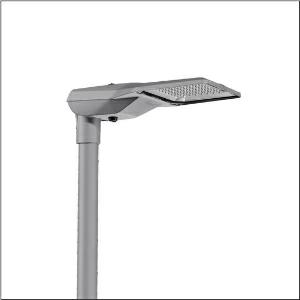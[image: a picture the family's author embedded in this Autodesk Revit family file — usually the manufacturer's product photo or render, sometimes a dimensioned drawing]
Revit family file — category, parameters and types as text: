
# Revit family: streetlight_sl_21_iq_midi___st1_0a_5xe3d61y08mb_8671
name_source: partatom
category: Lighting Fixtures
units: mm (PartAtom-declared; Revit-internal decimal feet)

## family parameters
Cut with Voids When Loaded = No
Host = Face
Light Source = No
Part Type = Normal
Room Calculation Point = No
Round Connector Dimension = Use Diameter
Shared = No

## types (1)
- --- (1 x LED, 15910 lm, 129.3 W, 2700K)
    Apparent Load = 129 VA
    CIE Flux Codes = 37 72 97 100 100
    Color Rendering = 70
    Color Temperature = 2700K
    Default Elevation = 1800 mm
    Description = Streetlight SL 21 iQ midi, mast luminaire, primary light control with lens, of PMMA, primary optical cover: cover, of toughened safety glass, transparent, light distribution: ST1.0a, light emission: direct distribution, primary light characteristic: asymmetric, installation type: post-top, side-entry, LED, High Power LED, rated luminous flux: 15.910lm, luminous efficacy: 123lm/W, light colour: 727, colour temperature: 2700K, control gear: iQ-Street Remote, D4i with power reduction, control: pre-setting: logarithmic dimming characteristic, Street-Remote, Auto-Match, Temp-Guard, Lumen-Switch, Night-Set, Smart-Wire, Light-Fading, Desk-Remote (wireless, voltage-free reading and setting of iQ features in the workshop via application-optimized NFC function/RFID function), optimised constant luminous flux control (CLO 2.0), mains connection: 230..240V, AC, 50/60Hz, start of lifetime: 129W, end of service life: 142W, reduction: 56W, luminaire housing, of diecast aluminium, powder-coated, SITECO metallic grey (DB 702S), corrosivity category C5 high according to DIN EN ISO 12944, please order mast flange separately, inclination adjustable: 0°, 5°, 10°, 15°, sealing non-destructively replaceable, multi-level sealing system, length: 644mm, width: 335mm, height: 110mm, mast flange for spigot size: 42mm (side-entry): 5XC10008XM4, 60/48mm (side-entry/post-top): 5XC10108XM2, 76/60mm (side-entry/post-top): 5XC10108XM1, mounting height: 4..8m, Smart Interface below and above, protection rating (complete): IP66, insulation class (complete): insulation class II (safety insulation), certification: CE, ENEC, ENEC+, VDE, impact resistance: IK10, permissible operating ambient temperature for outdoor applications: -40..+50°C, standard-compliant lighting for roads and squares, packaging unit: 1 piece

Light Distribution: ST1.0a
    Height = 111 mm
    Lamp = 1 x LED
    Lamp Light Flux = 15910 lm
    Lamp Power = 129.3 W
    Lamp count = 1
    Length = 644 mm
    Luminous efficacy = 123 lm/W
    Manufacturer = Siteco
    ModVariant = No
    Model = 5XE3D61Y08MB
    Mounting Place = Pole
    Mounting Type = Pole top
    Number of Poles = 1
    OnlyDefault = Yes
    Power Factor = 1
    Product Name = Streetlight SL 21 iQ midi | ST1.0a
    Product group = mast luminaire | pylon top
    ProductGroupID = 6100
    Protection Class = Protection class II
    Protection Degree = IP 66
    RLX_Detail_Level = 1
    RLX_Emergency_Light_Flux = 0 lm
    RLX_Emergency_Type = 0
    RLX_Emergency_Type_DB = No
    RlxData = <blob elided: 91133 chars, md5=a09c30ba>
    Socket = socket
    Standby Power = 0 W
    System Light Flux = 15910 lm
    System Power = 129 W
    Type Comments = factory setting: luminous flux: 100 % | dim-lin: 254 | 672 mA
    Type Image = l_1004304.jpg
    URL = http://relux.com
    VarID = @adj_116247
    Voltage = 0 V
    Weight = 0.00 kg
    Width = 336 mm

## geometry (parser evidence)
native form markers: Blend x4, Sweep x12
no freeform markers — native parametric forms only
